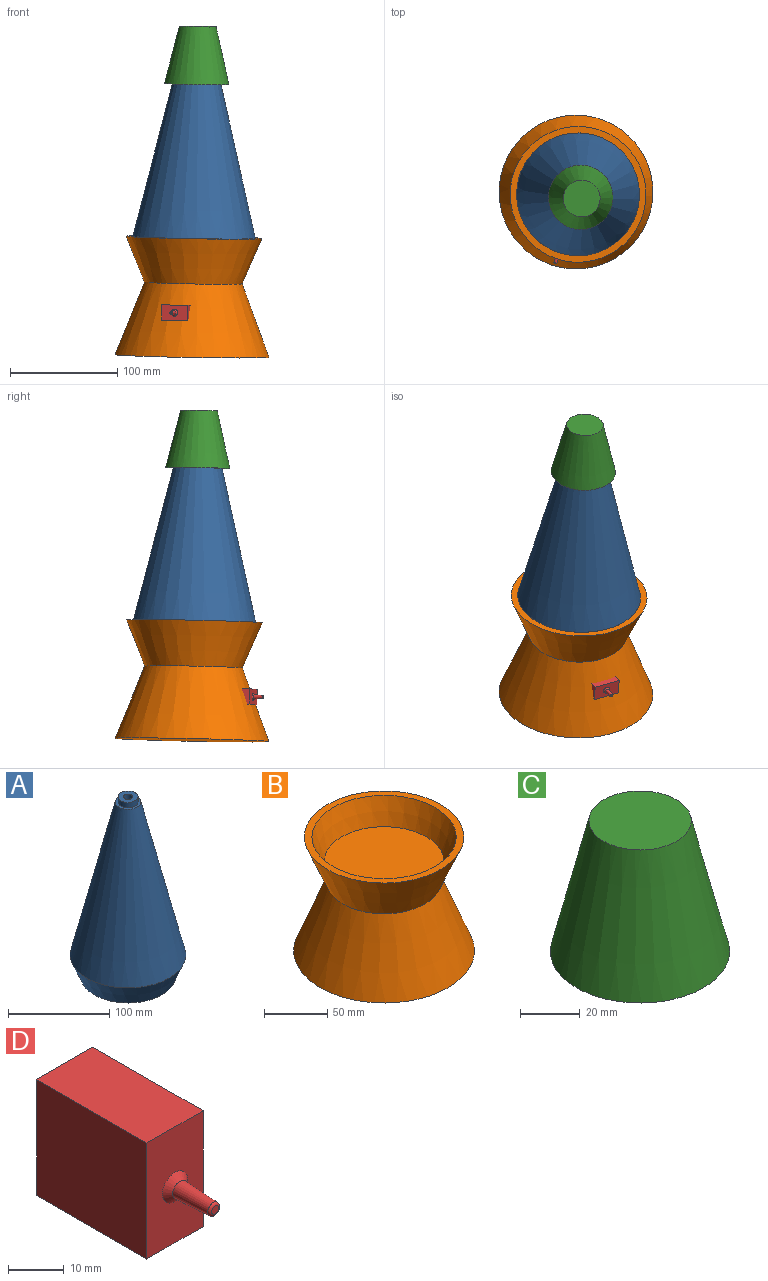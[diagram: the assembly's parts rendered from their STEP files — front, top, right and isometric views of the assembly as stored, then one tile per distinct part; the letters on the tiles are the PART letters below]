
ASSEMBLY  parts=4 mates=3
PART A: 12 faces, bbox 114.3x114.3x216.7 mm
  f0: plane 93.88x93.88mm, normal (0,0,-1), area 6922.8mm2, adj f1
  f1: cone r=57.15mm half-angle=21.9deg, axis (0,0,1), area 8951.9mm2, adj f0,f2
  f2: cone r=12.7mm half-angle=13.5deg, axis (0,0,-1), area 41733mm2, adj f1,f3
  f3: plane 25.4x25.4mm, normal (0,0,1), area 200mm2, adj f2,f5
  f4: cylinder r=4.45mm len=8.89mm, axis (0,0,-1), area 177.3mm2, adj f6,f7
  f5: cylinder r=9.88mm len=19.76mm, axis (0,0,-1), area 394.2mm2, adj f3,f6
  f6: plane 19.76x19.76mm, normal (0,0,1), area 244.6mm2, adj f4,f5
  f7: plane 8.89x8.89mm, normal (0,0,1), area 62.1mm2, adj f4
  f8: cone r=8.3mm half-angle=13.5deg, axis (0,0,-1), area 34590.2mm2, adj f9,f11
  f9: cone r=51.4mm half-angle=22.5deg, axis (0,0,1), area 6629mm2, adj f8,f10
  f10: plane 85.63x85.63mm, normal (0,0,1), area 5759mm2, adj f9
  f11: plane 16.59x16.59mm, normal (0,0,-1), area 216.2mm2, adj f8
PART B: 9 faces, bbox 143.3x143.3x110.4 mm
  f0: cone r=57.15mm half-angle=22.7deg, axis (0,0,1), area 8338.7mm2, adj f4,f5
  f1: plane 143.28x143.28mm, normal (0,0,-1), area 16124mm2, adj f2
  f2: cone r=45.46mm half-angle=21.1deg, axis (0,0,-1), area 26794.4mm2, adj f1,f3
  f3: cone r=63.21mm half-angle=22.7deg, axis (0,0,1), area 15703.5mm2, adj f2,f4
  f4: plane 126.41x126.41mm, normal (0,0,1), area 2290.3mm2, adj f0,f3
  f5: plane 94.7x94.7mm, normal (0,0,1), area 7043.3mm2, adj f0
  f6: plane 127x127mm, normal (0,0,1), area 12667.7mm2, adj f7
  f7: cone r=39.44mm half-angle=21.1deg, axis (0,0,-1), area 21646.9mm2, adj f6,f8
  f8: plane 78.87x78.87mm, normal (0,0,-1), area 4885.8mm2, adj f7
PART C: 5 faces, bbox 60x60x53.6 mm
  f0: plane 34.21x34.21mm, normal (0,0,1), area 919.1mm2, adj f4
  f1: plane 25.4x25.4mm, normal (0,0,-1), area 506.7mm2, adj f2
  f2: cone r=12.7mm half-angle=13.5deg, axis (0,0,-1), area 5724.2mm2, adj f1,f3
  f3: plane 59.96x59.96mm, normal (0,0,-1), area 978.8mm2, adj f2,f4
  f4: cone r=17.1mm half-angle=13.5deg, axis (0,0,-1), area 8147.7mm2, adj f0,f3
PART D: 10 faces, bbox 14.2x38.1x25.4 mm
  f0: plane 27.94x14.22mm, normal (0,0,1), area 397.4mm2, adj f1,f3,f4,f5
  f1: plane 27.94x25.4mm, normal (-1,0,0), area 709.7mm2, adj f0,f2,f4,f5
  f2: plane 27.94x14.22mm, normal (0,0,-1), area 397.4mm2, adj f1,f3,f4,f5
  f3: plane 27.94x25.4mm, normal (1,0,0), area 709.7mm2, adj f0,f2,f4,f5
  f4: plane 25.4x14.22mm, normal (0,-1,0), area 329.6mm2, adj f0,f1,f2,f3,f9
  f5: plane 25.4x14.22mm, normal (0,1,0), area 361.3mm2, adj f0,f1,f2,f3
  f6: cone r=1.91mm half-angle=3deg, axis (0,1,0), area 85.7mm2, adj f8,f9
  f7: plane 1.8x1.8mm, normal (0,-1,0), area 2.6mm2, adj f8
  f8: torus R=0.9mm, axis (0,-1,0), area 5.7mm2, adj f6,f7
  f9: cone r=1.84mm half-angle=46.5deg, axis (0,1,0), area 29mm2, adj f4,f6
PLACE A rot(axis=(0.06,0.06,-1),18.1deg) t=(361.27,-61.33,-394.32)mm
PLACE B rot(axis=(0.06,0.07,-1),16.8deg) t=(360.55,-60.45,-436.21)mm fixed
PLACE C rot(axis=(0.01,-0.01,1),138.6deg) t=(363.74,-64.36,-251.08)mm
PLACE D rot(axis=(0.15,0.98,-0.13),92.4deg) t=(386.75,-63.82,-463.7)mm
MATE slider B.f2 <-> D.f3  axis (-0.02,0.02,-1) through (359.96,-59.73,-470.26)mm
MATE cylindrical C.f2 <-> A.f5  axis (-0.02,0.02,-1) through (364.57,-65.37,-203.13)mm
MATE cylindrical A.f1 <-> B.f0  axis (-0.02,0.02,-1) through (360.83,-60.8,-419.71)mm
